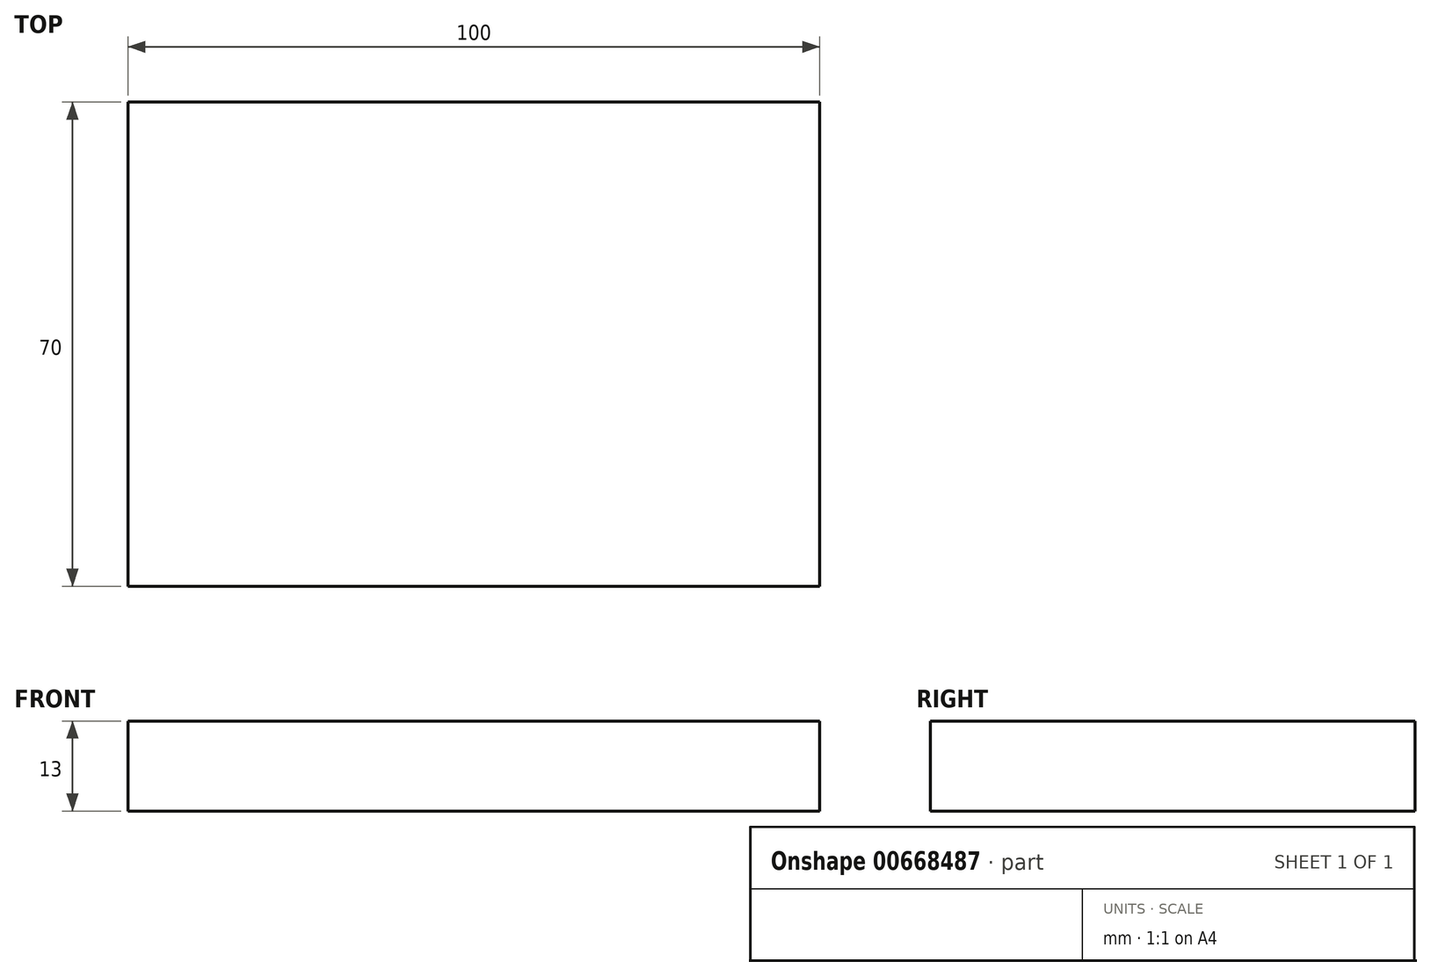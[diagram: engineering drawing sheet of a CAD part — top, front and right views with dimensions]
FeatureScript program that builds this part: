
annotation { "Feature Type Name" : "Feature", "Feature Type Description" : "" }
export const myFeature = defineFeature(function(context is Context, id is Id, definition is map)
    precondition{}
    {
        {
            var Q0;
            Q0=qCreatedBy(makeId("Top.planeOp"),FACE);
            var sketch = newSketch(context, id + "F0", { "sketchPlane" : qUnion([Q0])});
            skLineSegment(sketch, "E0.bottom", {"start": v(50, 35) * mm, "end": v(-50, 35) * mm});
            skLineSegment(sketch, "E0.top", {"start": v(50, -35) * mm, "end": v(-50, -35) * mm});
            skLineSegment(sketch, "E0.left", {"start": v(50, 35) * mm, "end": v(50, -35) * mm});
            skLineSegment(sketch, "E0.right", {"start": v(-50, 35) * mm, "end": v(-50, -35) * mm});
            skPoint(sketch, "E0.middle", {"position": v(0, 0) * mm});
            skSolve(sketch);
        }
        {
            var Q0;
            Q0 = qSketchRegion(id + "F0", true);
            extrude(context, id + "F1", {"entities" : qUnion([Q0]), "depth" : 13 * mm, "offsetDistance" : 25 * mm});
        }
    });
